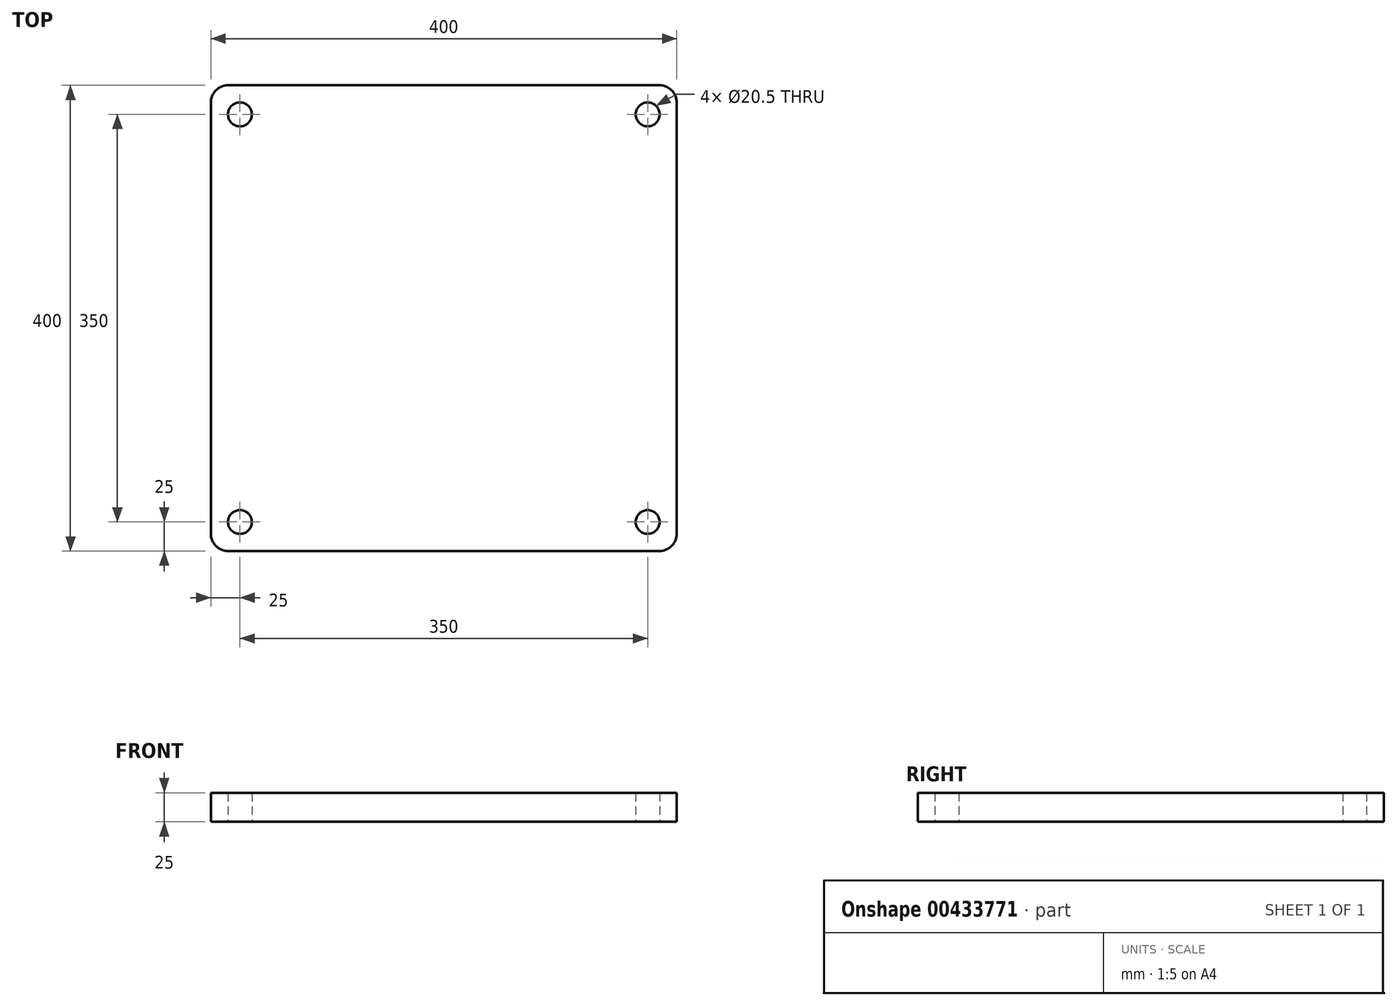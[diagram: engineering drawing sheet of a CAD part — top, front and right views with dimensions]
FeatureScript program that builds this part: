
annotation { "Feature Type Name" : "Feature", "Feature Type Description" : "" }
export const myFeature = defineFeature(function(context is Context, id is Id, definition is map)
    precondition{}
    {
        {
            var Q0;
            Q0=qCreatedBy(makeId("Top.planeOp"),FACE);
            var sketch = newSketch(context, id + "F0", { "sketchPlane" : qUnion([Q0])});
            skLineSegment(sketch, "E0.bottom", {"start": v(185, -200) * mm, "end": v(-185, -200) * mm});
            skLineSegment(sketch, "E0.top", {"start": v(185, 200) * mm, "end": v(-185, 200) * mm});
            skLineSegment(sketch, "E0.left", {"start": v(200, -185) * mm, "end": v(200, 185) * mm});
            skLineSegment(sketch, "E0.right", {"start": v(-200, -185) * mm, "end": v(-200, 185) * mm});
            skPoint(sketch, "E0.middle", {"position": v(0, 0) * mm});
            skPoint(sketch, "E1.visualSharp", {"position": v(-200, 200) * mm});
            skArc(sketch, "E1.filletArc", {"start": v(-185, 200) * mm, "mid": v(-195.6, 195.6) * mm, "end": v(-200, 185) * mm});
            skPoint(sketch, "E2.visualSharp", {"position": v(200, 200) * mm});
            skArc(sketch, "E2.filletArc", {"start": v(200, 185) * mm, "mid": v(195.6, 195.6) * mm, "end": v(185, 200) * mm});
            skPoint(sketch, "E3.visualSharp", {"position": v(200, -200) * mm});
            skArc(sketch, "E3.filletArc", {"start": v(185, -200) * mm, "mid": v(195.6, -195.6) * mm, "end": v(200, -185) * mm});
            skPoint(sketch, "E4.visualSharp", {"position": v(-200, -200) * mm});
            skArc(sketch, "E4.filletArc", {"start": v(-200, -185) * mm, "mid": v(-195.6, -195.6) * mm, "end": v(-185, -200) * mm});
            skLineSegment(sketch, "E5", {"start": v(-185, -185) * mm, "end": v(185, 185) * mm, "construction": true});
            skCircle(sketch, "E6", {"center": v(175, 175) * mm, "radius": 10.25 * mm});
            skCircle(sketch, "E7.1.1", {"center": v(-175, 175) * mm, "radius": 10.25 * mm});
            skCircle(sketch, "E7.2.1", {"center": v(-175, -175) * mm, "radius": 10.25 * mm});
            skCircle(sketch, "E7.3.1", {"center": v(175, -175) * mm, "radius": 10.25 * mm});
            skSolve(sketch);
        }
        {
            var Q0;
            Q0=qSketchRegion(id+"F0",true);
            extrude(context, id + "F1", {"entities" : qUnion([Q0]), "depth" : 25 * mm});
        }
    });
